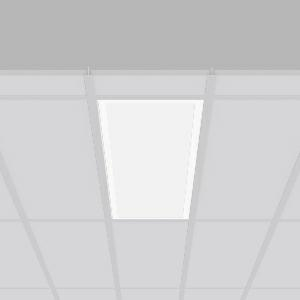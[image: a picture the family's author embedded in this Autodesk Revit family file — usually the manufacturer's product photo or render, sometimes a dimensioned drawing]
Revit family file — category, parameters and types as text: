
# Revit family: sidelite_eco_672376_002_89_b1d4
name_source: partatom
category: Lighting Fixtures
units: mm (PartAtom-declared; Revit-internal decimal feet)

## family parameters
Cut with Voids When Loaded = No
Host = Face
Light Source = No
Part Type = Normal
Room Calculation Point = No
Round Connector Dimension = Use Diameter
Shared = No

## types (1)
- SIDELITE ECO (1 x LED Modul 830, 3300 lm, 3000)
    Apparent Load = 30 VA
    CIE Flux Codes = 47 79 96 100 100
    Color Rendering = 80
    Color Temperature = 3000
    Default Elevation = 1800 mm
    Description = Series: SIDELITE ECO
Highly economical recessed luminaire with progressive LED technology. For escape route illumination. Frame made of aluminium, powder-coated. Diffuser: plastic, opal. Lightguide and diffuser made of non-yellowing plastic (PMMA). Lateral light emission (RZB SIDELITE technology) for homogeneous light distribution. External driver. Second cable inlet for loop through. With AC Control monitoring module for LUXIFAIR central battery units. External driver with simple plug-in locking system. Extended connection cable (1.90 m). 
Colour: white
Length: 1245 mm
Width: 308 mm
Cut-out length: 1220 mm
Cut-out width: 285 mm
Recess height: 160 mm
Luminaire: recess height: 40 mm
Weight: 4.19 kg
Operating mode: maintained power mode
Lamp: LED
Socket: without socket
Colour temperature: 3000K
Colour rendering index (CRI): 80
System power: 30 W
Rated luminous flux: 3300 lm
Luminous flux, emergency: 3300 lm
System power, emergency: 30 W
Control gear: Regulated power supply
Protection class: I
Type of protection: IP 20
    Height = 0 mm  [stored 0 ft]
    Lamp = 1 x LED Modul 830
    Lamp Light Flux = 3300 lm
    Lamp count = 1
    Length = 1245 mm
    Lifetime = 50000 h
    Luminous efficacy = 110 lm/W
    Manufacturer = RZB
    ModVariant = No
    Model = 672376.002.89
    Mounting Place = Ceiling
    Mounting Type = Recessed
    Number of Poles = 1
    OnlyDefault = Yes
    Power Factor = 1
    Product Name = SIDELITE ECO
    Product group = Recessed modular luminaires
    ProductGroupID = 406
    Protection Class = Protection class I
    Protection Degree = Degree of protection
    RLX_Detail_Level = 1
    RLX_Emergency_Light_Flux = 3300 lm
    RLX_Emergency_Type = 3
    RLX_Emergency_Type_DB = Yes
    RlxData = <blob elided: 30441 chars, md5=d3ed8df9>
    Socket = socket
    Standby Power = 0 W
    System Light Flux = 3300 lm
    System Power = 30 W
    Type Comments = Product without accessories
    Type Image = 312367.002.jpg
    URL = http://relux.com
    VarID = ---
    Voltage = 0 V
    Weight = 0.00 kg
    Width = 308 mm

note: [stored X ft] marks values corroborated as IEEE doubles in the binary element streams (Revit-internal decimal feet)

## geometry (parser evidence)
native form markers: Blend x4, Sweep x11
no freeform markers — native parametric forms only
